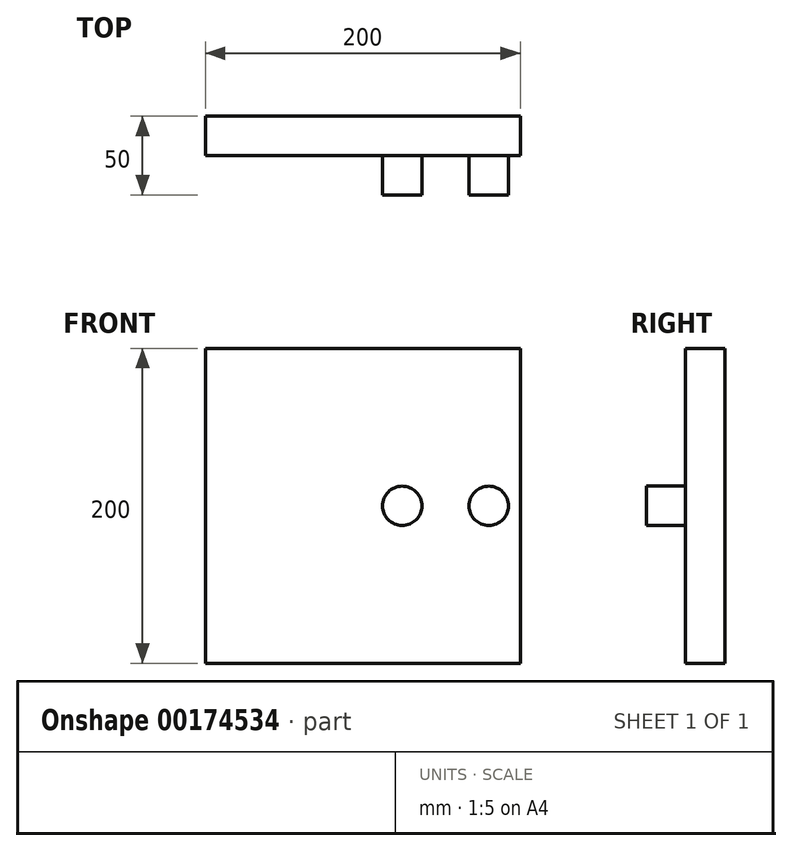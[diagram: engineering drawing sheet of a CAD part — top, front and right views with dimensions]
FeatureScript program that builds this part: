
annotation { "Feature Type Name" : "Feature", "Feature Type Description" : "" }
export const myFeature = defineFeature(function(context is Context, id is Id, definition is map)
    precondition{}
    {
        {
            var Q0;
            Q0=qCreatedBy(makeId("Front.planeOp"),FACE);
            var sketch = newSketch(context, id + "F0", { "sketchPlane" : qUnion([Q0])});
            skLineSegment(sketch, "E0.bottom", {"start": v(100, 100) * mm, "end": v(-100, 100) * mm});
            skLineSegment(sketch, "E0.top", {"start": v(100, -100) * mm, "end": v(-100, -100) * mm});
            skLineSegment(sketch, "E0.left", {"start": v(100, 100) * mm, "end": v(100, -100) * mm});
            skLineSegment(sketch, "E0.right", {"start": v(-100, 100) * mm, "end": v(-100, -100) * mm});
            skPoint(sketch, "E0.middle", {"position": v(0, 0) * mm});
            skSolve(sketch);
        }
        {
            var Q0;
            Q0=makeQuery(id+"F0.imprint","IMPRINT",FACE,{"disambiguationData":[TD([[makeQuery(id+"F0.imprint","IMPRINT",EDGE,{"derivedFrom":sQuery(id+"F0.wireOp",EDGE,"E0.bottom")}),1.0]])]});
            extrude(context, id + "F1", {"entities" : qUnion([Q0]), "depth" : 25 * mm});
        }
        {
            var Q0;
            Q0=makeQuery(id+"F1.opExtrude","CAP_FACE",FACE,{"disambiguationData":[OSD([sQuery(id+"F0.wireOp",EDGE,"E0.bottom"),sQuery(id+"F0.wireOp",EDGE,"E0.top"),sQuery(id+"F0.wireOp",EDGE,"E0.left"),sQuery(id+"F0.wireOp",EDGE,"E0.right")])],"isStart":false});
            var sketch = newSketch(context, id + "F2", { "sketchPlane" : qUnion([Q0])});
            skCircle(sketch, "E1", {"center": v(25, 0) * mm, "radius": 12.5 * mm});
            skCircle(sketch, "E2", {"center": v(80, 0) * mm, "radius": 12.5 * mm});
            skSolve(sketch);
        }
        {
            var Q0;
            Q0 = qSketchRegion(id + "F2", true);
            extrude(context, id + "F3", {"entities" : qUnion([Q0]), "operationType" : NewBodyOperationType.ADD, "depth" : 25 * mm});
        }
    });
